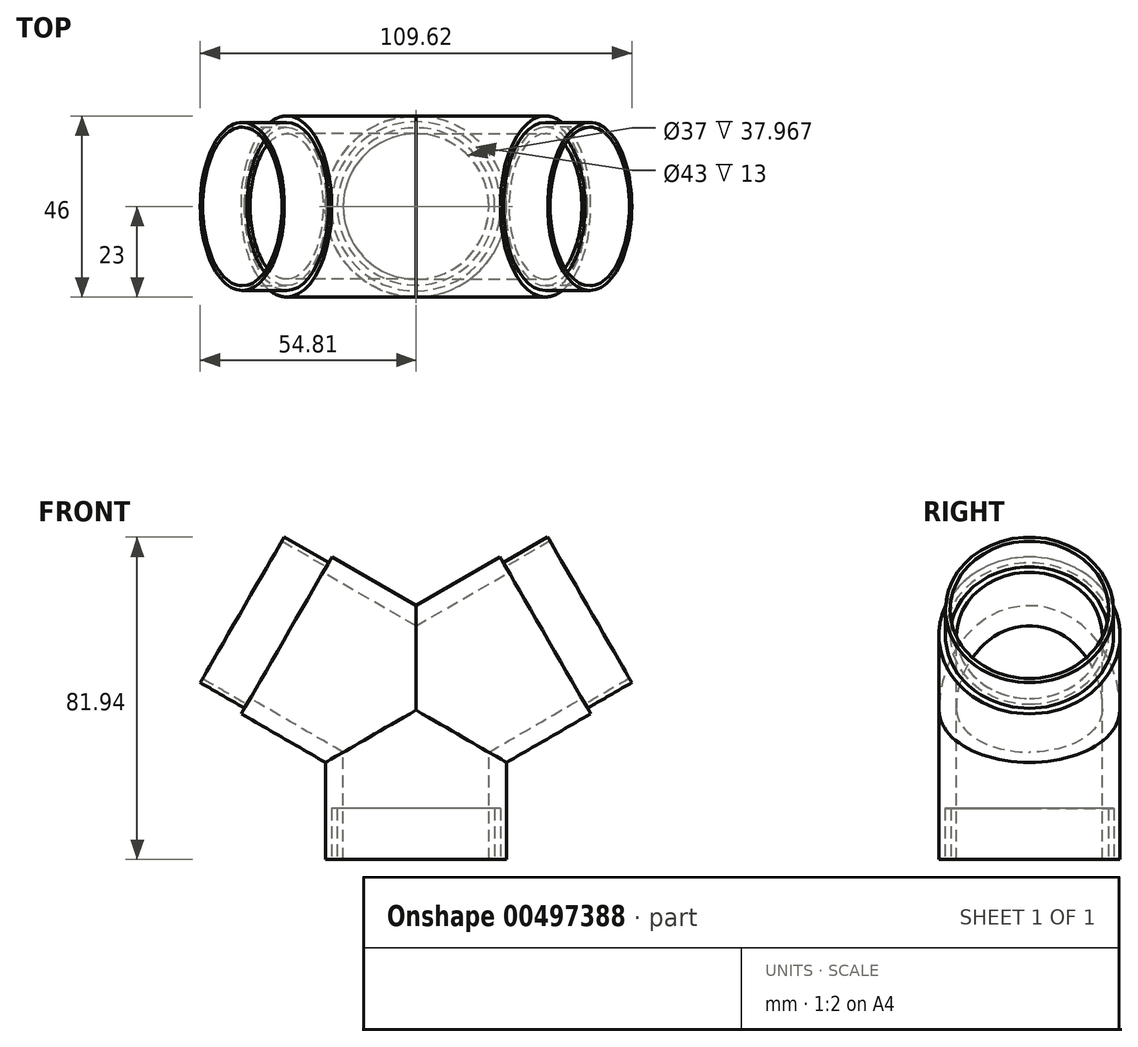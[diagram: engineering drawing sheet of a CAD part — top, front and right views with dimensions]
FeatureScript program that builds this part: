
annotation { "Feature Type Name" : "Feature", "Feature Type Description" : "" }
export const myFeature = defineFeature(function(context is Context, id is Id, definition is map)
    precondition{}
    {
        {
            var Q0;
            Q0=qCreatedBy(makeId("Front.planeOp"),FACE);
            var sketch = newSketch(context, id + "F0", { "sketchPlane" : qUnion([Q0])});
            skLineSegment(sketch, "E0", {"start": v(0, 0) * mm, "end": v(0, 37.97) * mm});
            skLineSegment(sketch, "E1", {"start": v(0, 37.97) * mm, "end": v(32.88, 56.95) * mm});
            skSolve(sketch);
        }
        {
            var Q0;
            Q0=qCreatedBy(makeId("Top.planeOp"),FACE);
            var sketch = newSketch(context, id + "F1", { "sketchPlane" : qUnion([Q0])});
            skPoint(sketch, "E2.0", {"position": v(0, 0) * mm});
            skCircle(sketch, "E3", {"center": v(0, 0) * mm, "radius": 23 * mm});
            skCircle(sketch, "E4.0", {"center": v(0, 0) * mm, "radius": 21.5 * mm});
            skCircle(sketch, "E5.0", {"center": v(0, 0) * mm, "radius": 20 * mm});
            skCircle(sketch, "E6.0", {"center": v(0, 0) * mm, "radius": 18.5 * mm});
            skSolve(sketch);
        }
        {
            var Q0;
            Q0=makeQuery(id+"F1.imprint","IMPRINT",FACE,{"disambiguationData":[TD([[makeQuery(id+"F1.imprint","IMPRINT",EDGE,{"derivedFrom":sQuery(id+"F1.wireOp",EDGE,"E3")}),1.0]])]});
            var Q1;
            Q1=makeQuery(id+"F1.imprint","IMPRINT",FACE,{"disambiguationData":[TD([[makeQuery(id+"F1.imprint","IMPRINT",EDGE,{"derivedFrom":sQuery(id+"F1.wireOp",EDGE,"E5.0")}),1.0]])]});
            var Q2;
            Q2=makeQuery(id+"F1.imprint","IMPRINT",FACE,{"disambiguationData":[TD([[makeQuery(id+"F1.imprint","IMPRINT",EDGE,{"derivedFrom":sQuery(id+"F1.wireOp",EDGE,"E4.0")}),1.0]])]});
            var Q3;
            Q3=sQuery(id+"F0.wireOp",EDGE,"E0");
            var Q4;
            Q4=sQuery(id+"F0.wireOp",EDGE,"E1");
            sweep(context, id + "F2", {"profiles" : qUnion([Q0, Q1, Q2]), "path" : qUnion([Q3, Q4])});
        }
        {
            var Q0;
            Q0=makeQuery(id+"F2.opSweep","CAP_FACE",FACE,{"disambiguationData":[OSD([sQuery(id+"F0.wireOp",VERTEX,"E1.end"),sQuery(id+"F1.wireOp",EDGE,"E3"),sQuery(id+"F1.wireOp",EDGE,"E6.0")])],"isStart":false});
            var sketch = newSketch(context, id + "F3", { "sketchPlane" : qUnion([Q0])});
            skCircle(sketch, "E7.0", {"center": v(0, 32.88) * mm, "radius": 23 * mm});
            skCircle(sketch, "E8.0", {"center": v(0, 32.88) * mm, "radius": 18.5 * mm});
            skCircle(sketch, "E9", {"center": v(0, 32.88) * mm, "radius": 21.35 * mm});
            skCircle(sketch, "E10", {"center": v(0, 32.88) * mm, "radius": 20.15 * mm});
            skSolve(sketch);
        }
        {
            var Q0;
            Q0=makeQuery(id+"F3.imprint","IMPRINT",FACE,{"disambiguationData":[TD([[makeQuery(id+"F3.imprint","IMPRINT",EDGE,{"derivedFrom":sQuery(id+"F3.wireOp",EDGE,"E9")}),1.0]])]});
            extrude(context, id + "F4", {"entities" : qUnion([Q0]), "operationType" : NewBodyOperationType.ADD, "depth" : 13 * mm});
        }
        {
            var Q0;
            Q0=makeQuery(id+"F1.imprint","IMPRINT",FACE,{"disambiguationData":[TD([[makeQuery(id+"F1.imprint","IMPRINT",EDGE,{"derivedFrom":sQuery(id+"F1.wireOp",EDGE,"E4.0")}),1.0]])]});
            extrude(context, id + "F5", {"entities" : qUnion([Q0]), "operationType" : NewBodyOperationType.REMOVE, "depth" : 13 * mm, "offsetDistance" : 25.4 * mm});
        }
        {
            var Q0;
            Q0=makeQuery(id+"F2.opSweep","SWEPT_BODY",BODY,{"disambiguationData":[OSD([sQuery(id+"F0.wireOp",EDGE,"E1"),sQuery(id+"F1.wireOp",EDGE,"E3"),sQuery(id+"F1.wireOp",EDGE,"E6.0")])]});
            var Q1;
            Q1=qCreatedBy(makeId("Right.planeOp"),FACE);
            mirror(context, id + "F6", {"operationType" : NewBodyOperationType.ADD, "entities" : qUnion([Q0]), "mirrorPlane" : qUnion([Q1])});
        }
        {
            var Q0;
            Q0=makeQuery(id+"F3.imprint","IMPRINT",FACE,{"disambiguationData":[TD([[makeQuery(id+"F3.imprint","IMPRINT",EDGE,{"derivedFrom":sQuery(id+"F3.wireOp",EDGE,"E8.0")}),-1.0]])]});
            extrude(context, id + "F7", {"entities" : qUnion([Q0]), "oppositeDirection" : true, "depth" : 38.1 * mm, "offsetDistance" : 25.4 * mm});
        }
        {
            var Q0;
            Q0=makeQuery(id+"F7.opExtrude","SWEPT_BODY",BODY,{"disambiguationData":[OSD([sQuery(id+"F3.wireOp",EDGE,"E8.0")])]});
            var Q1;
            Q1=qCreatedBy(makeId("Right.planeOp"),FACE);
            mirror(context, id + "F8", {"operationType" : NewBodyOperationType.REMOVE, "entities" : qUnion([Q0]), "mirrorPlane" : qUnion([Q1])});
        }
        {
            var Q0;
            Q0=makeQuery(id+"F3.imprint","IMPRINT",FACE,{"disambiguationData":[TD([[makeQuery(id+"F3.imprint","IMPRINT",EDGE,{"derivedFrom":sQuery(id+"F3.wireOp",EDGE,"E8.0")}),-1.0]])]});
            extrude(context, id + "F9", {"entities" : qUnion([Q0]), "operationType" : NewBodyOperationType.REMOVE, "oppositeDirection" : true, "depth" : 38.1 * mm, "offsetDistance" : 25.4 * mm});
        }
    });
